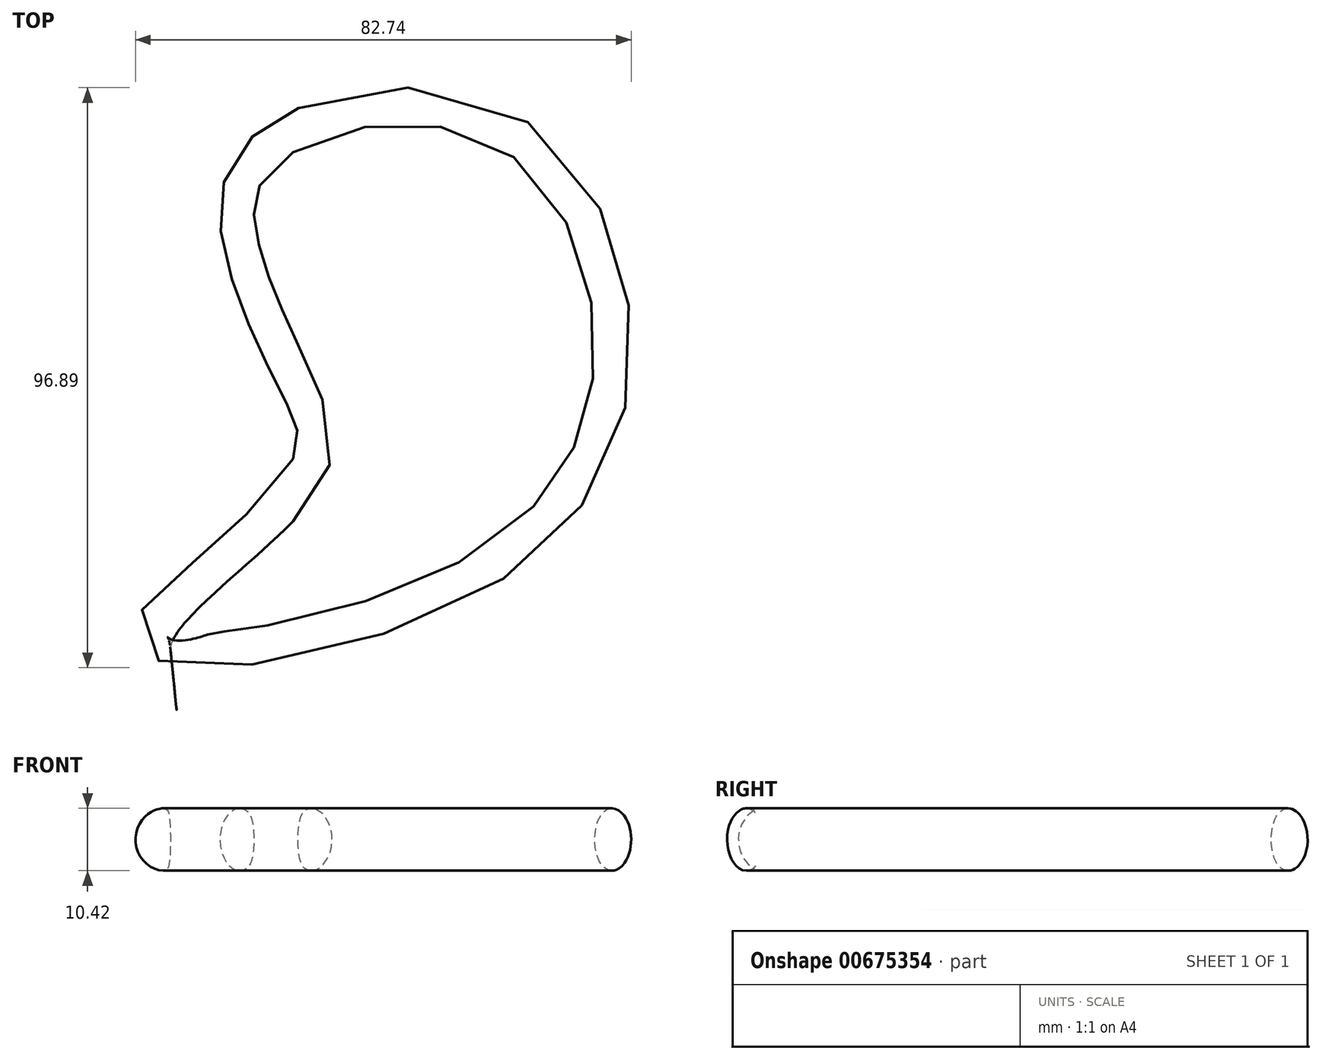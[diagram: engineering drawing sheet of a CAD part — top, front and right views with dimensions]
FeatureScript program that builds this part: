
annotation { "Feature Type Name" : "Feature", "Feature Type Description" : "" }
export const myFeature = defineFeature(function(context is Context, id is Id, definition is map)
    precondition{}
    {
        {
            var Q0;
            Q0=qCreatedBy(makeId("Top.planeOp"),FACE);
            var sketch = newSketch(context, id + "F0", { "sketchPlane" : qUnion([Q0])});
            skFitSpline(sketch, "E0", {"points": [v(0, 0) * mm, v(0, 18.8) * mm, v(-7.12, 52.95) * mm, v(33.18, 61.04) * mm, v(53.2, 21.8) * mm, v(26.55, -16) * mm, v(-21.59, -24) * mm, v(0, 0) * mm]});
            skSolve(sketch);
        }
        {
            var Q0;
            Q0=qCreatedBy(makeId("Right.planeOp"),FACE);
            var sketch = newSketch(context, id + "F1", { "sketchPlane" : qUnion([Q0])});
            skCircle(sketch, "E1", {"center": v(0, 0) * mm, "radius": 5.21 * mm});
            skSolve(sketch);
        }
        {
            var Q0;
            Q0=makeQuery(id+"F1.imprint","IMPRINT",FACE,{"disambiguationData":[TD([[makeQuery(id+"F1.imprint","IMPRINT",EDGE,{"derivedFrom":sQuery(id+"F1.wireOp",EDGE,"E1")}),1.0]])]});
            var Q1;
            Q1=sQuery(id+"F0.wireOp",EDGE,"E0");
            sweep(context, id + "F2", {"profiles" : qUnion([Q0]), "path" : qUnion([Q1])});
        }
    });
